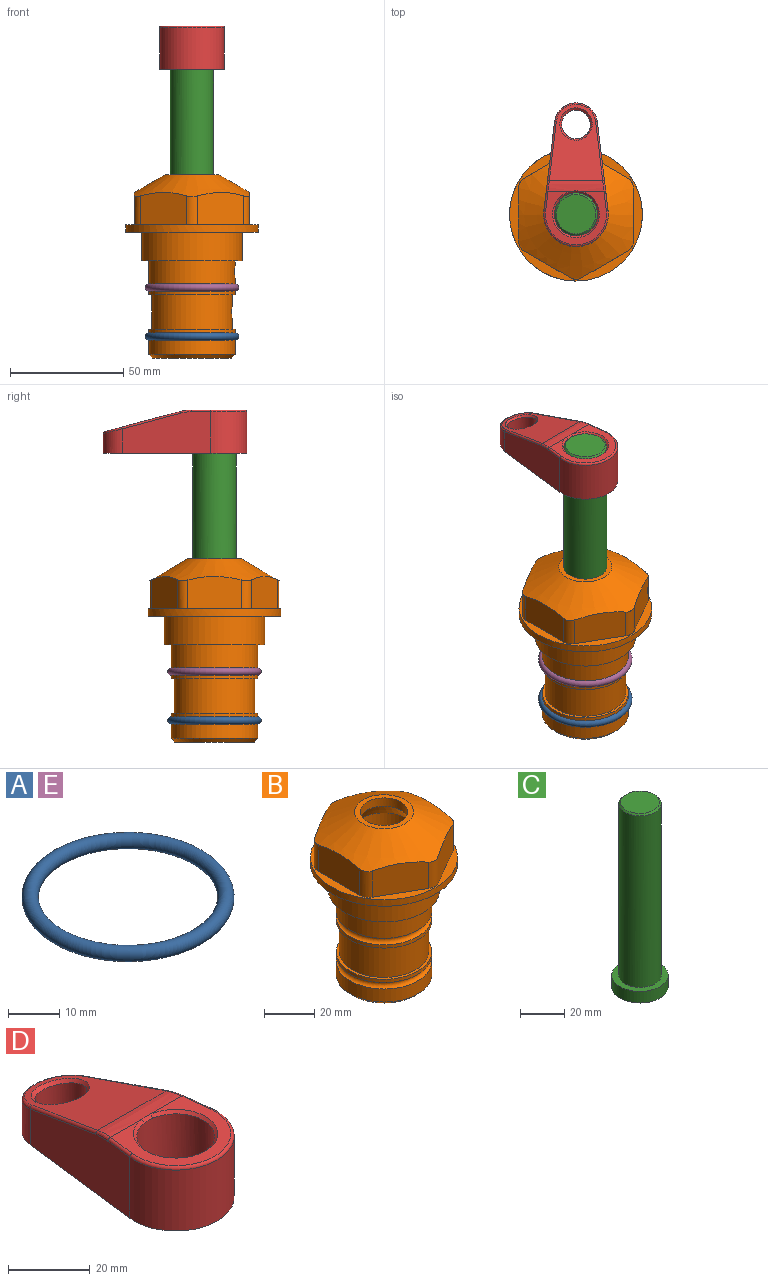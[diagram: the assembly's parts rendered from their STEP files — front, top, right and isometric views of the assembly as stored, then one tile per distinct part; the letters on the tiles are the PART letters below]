
ASSEMBLY  parts=5 mates=4
PART A: 1 faces, bbox 44.7x44.7x3.2 mm
  f0: torus R=19.05mm, axis (0,0,1), area 1193.9mm2
PART B: 36 faces, bbox 58.7x58.7x81 mm
  f0: cylinder r=17.78mm len=35.56mm, axis (0,0,1), area 1670.8mm2, adj f23,f24,f31
  f1: cylinder r=19.05mm len=38.1mm, axis (0,0,1), area 1191.9mm2, adj f26,f27,f30
  f2: plane 58.66x58.66mm, normal (0,0,-1), area 1150.6mm2, adj f3,f28
  f3: cylinder r=29.33mm len=58.66mm, axis (0,0,-1), area 585.1mm2, adj f2,f4
  f4: plane 58.66x58.66mm, normal (0,0,1), area 475.9mm2, adj f3,f5,f6,f7,f8,f9,f10,f11
  f5: plane 20.32x14.34mm, normal (-0.5,0.87,0), area 324.4mm2, adj f4,f15,f16,f17
  f6: plane 20.32x14.34mm, normal (0.5,0.87,0), area 324.4mm2, adj f4,f14,f15,f17
  f7: plane 23.48x14.34mm, normal (1,0,0), area 324.4mm2, adj f4,f13,f14,f17
  f8: plane 20.32x14.34mm, normal (0.5,-0.87,0), area 324.4mm2, adj f4,f12,f13,f17
  f9: plane 20.32x14.34mm, normal (-0.5,-0.87,0), area 324.4mm2, adj f4,f11,f12,f17
  f10: plane 23.48x14.34mm, normal (-1,0,0), area 324.4mm2, adj f4,f11,f16,f17
  f11: cylinder r=5.08mm len=12.85mm, axis (0,0,-1), area 67.2mm2, adj f4,f9,f10,f17
  f12: cylinder r=5.08mm len=12.85mm, axis (0,0,-1), area 67.2mm2, adj f4,f8,f9,f17
  f13: cylinder r=5.08mm len=12.85mm, axis (0,0,-1), area 67.2mm2, adj f4,f7,f8,f17
  f14: cylinder r=5.08mm len=12.85mm, axis (0,0,-1), area 67.2mm2, adj f4,f6,f7,f17
  f15: cylinder r=5.08mm len=12.85mm, axis (0,0,-1), area 67.2mm2, adj f4,f5,f6,f17
  f16: cylinder r=5.08mm len=12.85mm, axis (0,0,-1), area 67.2mm2, adj f4,f5,f10,f17
  f17: cone r=11.73mm half-angle=60deg, axis (0,0,-1), area 2071.8mm2, adj f5,f6,f7,f8,f9,f10,f11,f12
  f18: plane 23.46x23.46mm, normal (0,0,1), area 147.4mm2, adj f17,f35
  f19: plane 34.93x34.93mm, normal (0,0,-1), area 958mm2, adj f29
  f20: cylinder r=19.05mm len=38.1mm, axis (0,0,1), area 760.1mm2, adj f21,f29
  f21: torus R=19.05mm, axis (0,0,1), area 565.3mm2, adj f20,f22
  f22: cylinder r=19.05mm len=38.1mm, axis (0,0,1), area 190mm2, adj f21,f23
  f23: plane 38.1x38.1mm, normal (0,0,1), area 146.9mm2, adj f0,f22
  f24: plane 38.1x38.1mm, normal (0,0,-1), area 146.9mm2, adj f0,f25
  f25: cylinder r=19.05mm len=38.1mm, axis (0,0,1), area 190mm2, adj f24,f26
  f26: torus R=19.05mm, axis (0,0,1), area 565.3mm2, adj f1,f25
  f27: plane 44.45x44.45mm, normal (0,0,-1), area 411.7mm2, adj f1,f28
  f28: cylinder r=22.23mm len=44.45mm, axis (0,0,1), area 1773.5mm2, adj f2,f27
  f29: cone r=19.05mm half-angle=45deg, axis (0,0,1), area 257.5mm2, adj f19,f20
  f30: cylinder r=3.17mm len=6.75mm, axis (-1,0,0), area 128mm2, adj f1,f33
  f31: cylinder r=3.17mm len=6.35mm, axis (-1,0,0), area 102.5mm2, adj f0,f33
  f32: plane 25.4x25.4mm, normal (0,0,1), area 506.7mm2, adj f33
  f33: cylinder r=12.7mm len=66.42mm, axis (0,0,-1), area 5236.2mm2, adj f30,f31,f32,f34
  f34: cone r=9.53mm half-angle=30deg, axis (0,0,-1), area 443.4mm2, adj f33,f35
  f35: cylinder r=9.53mm len=19.05mm, axis (0,0,-1), area 240.9mm2, adj f18,f34
PART C: 6 faces, bbox 25.4x25.4x101.6 mm
  f0: plane 17.46x17.46mm, normal (0,0,1), area 239.5mm2, adj f5
  f1: plane 25.4x25.4mm, normal (0,0,-1), area 506.7mm2, adj f2
  f2: cylinder r=12.7mm len=25.4mm, axis (0,0,1), area 506.7mm2, adj f1,f3
  f3: plane 25.4x25.4mm, normal (0,0,1), area 221.7mm2, adj f2,f4
  f4: cylinder r=9.53mm len=94.46mm, axis (0,0,1), area 5653mm2, adj f3,f5
  f5: cone r=8.73mm half-angle=45deg, axis (0,0,-1), area 64.4mm2, adj f0,f4
PART D: 31 faces, bbox 31.7x65.5x19.8 mm
  f0: plane 39.12x18.26mm, normal (0.99,0.12,0), area 612.2mm2, adj f1,f4,f7,f11,f13,f15
  f1: cylinder r=9.53mm len=18.91mm, axis (0,0,-1), area 296.1mm2, adj f0,f2,f7,f17
  f2: plane 39.12x18.26mm, normal (-0.99,0.12,0), area 612.2mm2, adj f1,f4,f7,f12,f14,f16
  f3: cylinder r=6.35mm len=12.7mm, axis (0,0,-1), area 362.4mm2, adj f7,f18
  f4: cylinder r=14.29mm len=28.58mm, axis (0,0,-1), area 882.2mm2, adj f0,f2,f7,f10
  f5: cylinder r=9.53mm len=19.05mm, axis (0,0,-1), area 1092.6mm2, adj f7,f19,f20
  f6: plane 26.99x23.69mm, normal (0,0,1), area 216.2mm2, adj f9,f10,f11,f12,f19
  f7: plane 63.5x28.58mm, normal (0,0,-1), area 661.8mm2, adj f0,f1,f2,f3,f4,f5,f22,f23
  f8: plane 33.52x23.6mm, normal (0,0.26,0.97), area 486mm2, adj f9,f15,f16,f17,f18
  f9: cylinder r=19.05mm len=24.72mm, axis (1,0,0), area 120.4mm2, adj f6,f8,f13,f14,f20
  f10: torus R=13.49mm, axis (0,0,1), area 59mm2, adj f4,f6,f11,f12
  f11: cylinder r=0.79mm len=8.67mm, axis (0.12,-0.99,0), area 10.8mm2, adj f0,f6,f10,f13
  f12: cylinder r=0.79mm len=8.67mm, axis (0.12,0.99,0), area 10.8mm2, adj f2,f6,f10,f14
  f13: bspline ~4.95x1.42mm, area 6.1mm2, adj f0,f9,f11,f15
  f14: bspline ~4.95x1.42mm, area 6.1mm2, adj f2,f9,f12,f16
  f15: cylinder r=0.79mm len=25.95mm, axis (0.12,-0.96,0.26), area 32.9mm2, adj f0,f8,f13,f17
  f16: cylinder r=0.79mm len=25.95mm, axis (0.12,0.96,-0.26), area 32.9mm2, adj f2,f8,f14,f17
  f17: bspline ~18.91x8.38mm, area 30mm2, adj f1,f8,f15,f16
  f18: bspline ~14.29x14.29mm, area 48.3mm2, adj f3,f8
  f19: cone r=9.53mm half-angle=45deg, axis (0,0,1), area 66.5mm2, adj f5,f6,f20
  f20: bspline ~3.22x0.96mm, area 3.5mm2, adj f5,f9,f19
  f21: plane 2.75x2.72mm, normal (0,0,-1), area 2.9mm2, adj f23,f25,f28
  f22: plane 23.05x15.88mm, normal (-0.99,-0.12,0), area 323.6mm2, adj f7,f25,f26,f27,f28,f29
  f23: plane 23.05x15.88mm, normal (0.99,-0.12,0), area 323.6mm2, adj f7,f21,f25,f27,f28,f30
  f24: cylinder r=9.53mm len=10.69mm, axis (0,0,-1), area 114.7mm2, adj f7,f27,f29,f30
  f25: cylinder r=12.7mm len=20.59mm, axis (0,0,-1), area 381.1mm2, adj f7,f21,f22,f23,f26,f28
  f26: plane 2.75x2.72mm, normal (0,0,-1), area 2.9mm2, adj f22,f25,f28
  f27: plane 19.72x18.37mm, normal (0,-0.26,-0.97), area 291.8mm2, adj f22,f23,f24,f28,f29,f30
  f28: cylinder r=15.88mm len=19.92mm, axis (1,0,0), area 54.8mm2, adj f21,f22,f23,f25,f26,f27
  f29: cylinder r=1.59mm len=11mm, axis (0,0,-1), area 34.7mm2, adj f7,f22,f24,f27
  f30: cylinder r=1.59mm len=11mm, axis (0,0,-1), area 34.7mm2, adj f7,f23,f24,f27
PART E: same geometry as A
PLACE A t=(0,0,-21.59)mm
PLACE B at identity fixed
PLACE C t=(0,0,27.55)mm
PLACE D t=(0,0,27.55)mm
PLACE E at identity
MATE cylindrical C.f2 <-> B.f0  axis (0,0,-1) through (0,0,-10.55)mm
MATE fastened A.f0 <-> B.f0  axis (0,0,1) through (0,0,-46.1)mm
MATE fastened D.f4 <-> C.f2  axis (0,0,-1) through (0,0,90.26)mm
MATE fastened E.f0 <-> B.f0  axis (0,0,1) through (0,0,-24.51)mm
